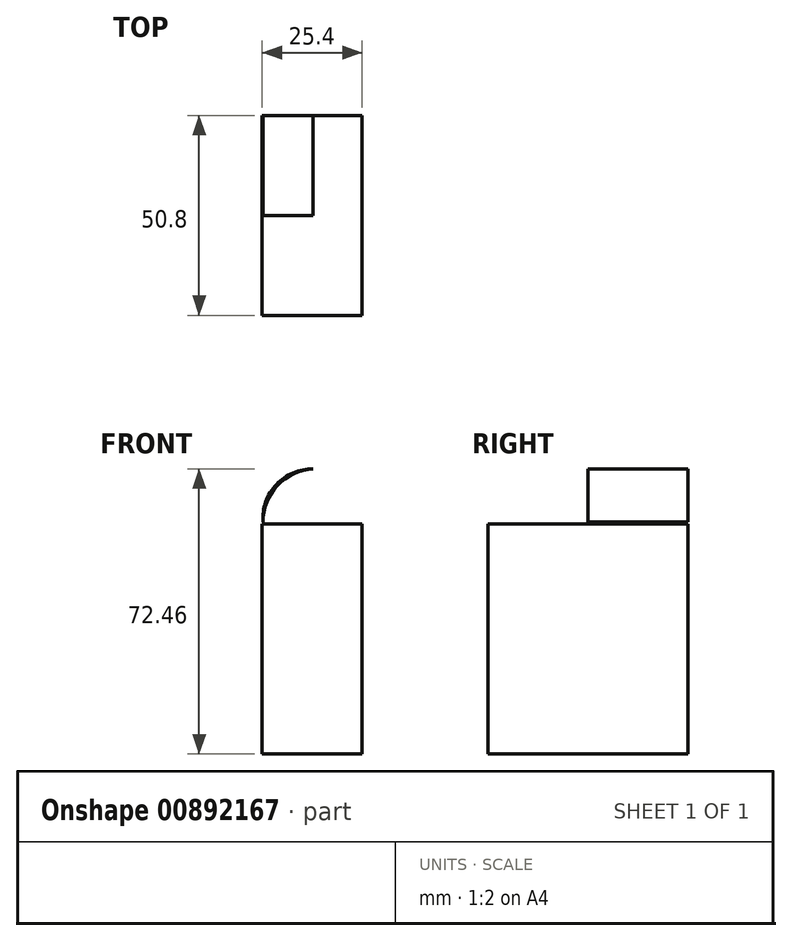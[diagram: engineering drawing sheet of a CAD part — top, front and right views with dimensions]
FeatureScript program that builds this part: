
annotation { "Feature Type Name" : "Feature", "Feature Type Description" : "" }
export const myFeature = defineFeature(function(context is Context, id is Id, definition is map)
    precondition{}
    {
        {
            var Q0;
            Q0=qCreatedBy(makeId("Front.planeOp"),FACE);
            var sketch = newSketch(context, id + "F0", { "sketchPlane" : qUnion([Q0])});
            skLineSegment(sketch, "E0.bottom", {"start": v(-12.93, 58.42) * mm, "end": v(12.47, 58.42) * mm});
            skLineSegment(sketch, "E0.top", {"start": v(-12.93, 0) * mm, "end": v(12.47, 0) * mm});
            skLineSegment(sketch, "E0.left", {"start": v(-12.93, 58.42) * mm, "end": v(-12.93, 0) * mm});
            skLineSegment(sketch, "E0.right", {"start": v(12.47, 58.42) * mm, "end": v(12.47, 0) * mm});
            skSolve(sketch);
        }
        {
            var Q0;
            Q0=makeQuery(id+"F0.imprint","IMPRINT",FACE,{"disambiguationData":[TD([[makeQuery(id+"F0.imprint","IMPRINT",EDGE,{"derivedFrom":sQuery(id+"F0.wireOp",EDGE,"E0.bottom")}),-1.0]])]});
            extrude(context, id + "F1", {"entities" : qUnion([Q0]), "depth" : 25.4 * mm, "offsetDistance" : 25.4 * mm});
        }
        {
            var Q0;
            Q0=qCreatedBy(makeId("Front.planeOp"),FACE);
            var sketch = newSketch(context, id + "F2", { "sketchPlane" : qUnion([Q0])});
            skArc(sketch, "E1", {"start": v(0, 72.46) * mm, "mid": v(-9.27, 68) * mm, "end": v(-12.7, 58.3) * mm});
            skArc(sketch, "E2", {"start": v(12.7, 58.72) * mm, "mid": v(9.4, 68.42) * mm, "end": v(0, 72.46) * mm});
            skArc(sketch, "E3.MirrorCS", {"start": v(-12.7, 58.72) * mm, "mid": v(-9.4, 68.42) * mm, "end": v(0, 72.46) * mm});
            skSolve(sketch);
        }
        {
            var Q0;
            Q0 = qSketchRegion(id + "F2", true);
            var Q1;
            Q1=makeQuery(id+"F1.opExtrude","CAP_FACE",FACE,{"disambiguationData":[OSD([sQuery(id+"F0.wireOp",EDGE,"E0.bottom"),sQuery(id+"F0.wireOp",EDGE,"E0.top"),sQuery(id+"F0.wireOp",EDGE,"E0.left"),sQuery(id+"F0.wireOp",EDGE,"E0.right")])],"isStart":false});
            extrude(context, id + "F3", {"entities" : qUnion([Q0, Q1]), "operationType" : NewBodyOperationType.ADD, "depth" : 25.4 * mm, "offsetDistance" : 25.4 * mm});
        }
    });
